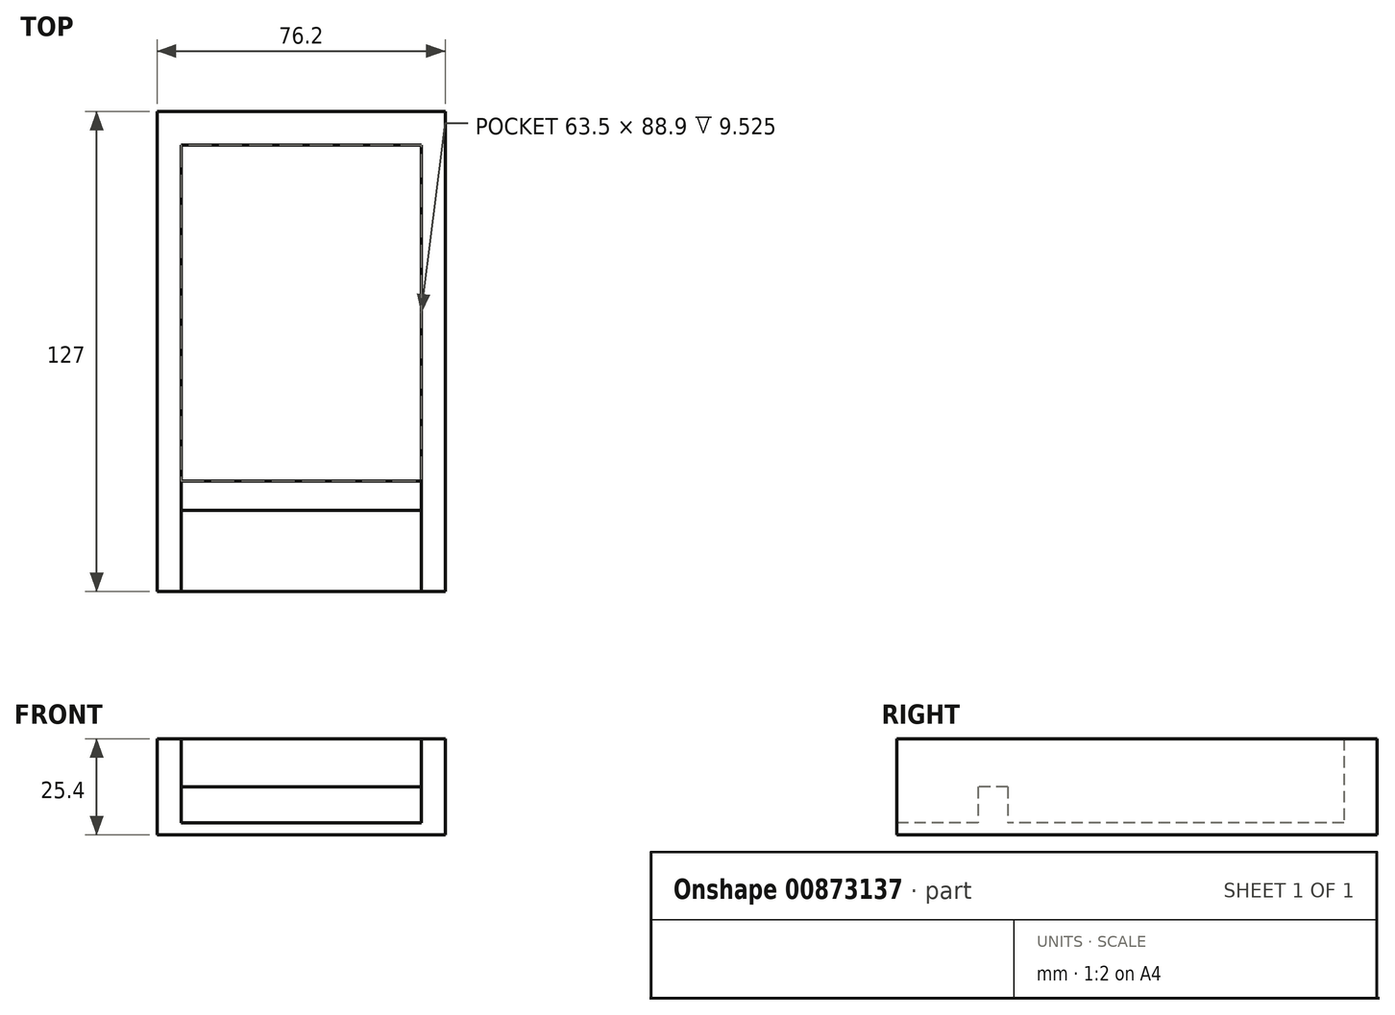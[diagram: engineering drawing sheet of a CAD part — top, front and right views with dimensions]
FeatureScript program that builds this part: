
annotation { "Feature Type Name" : "Feature", "Feature Type Description" : "" }
export const myFeature = defineFeature(function(context is Context, id is Id, definition is map)
    precondition{}
    {
        {
            var Q0;
            Q0=qCreatedBy(makeId("Top.planeOp"),FACE);
            var sketch = newSketch(context, id + "F0", { "sketchPlane" : qUnion([Q0])});
            skLineSegment(sketch, "E0.bottom", {"start": v(31.75, 44.45) * mm, "end": v(-31.75, 44.45) * mm});
            skLineSegment(sketch, "E0.top", {"start": v(31.75, -44.45) * mm, "end": v(-31.75, -44.45) * mm});
            skLineSegment(sketch, "E0.left", {"start": v(31.75, 44.45) * mm, "end": v(31.75, -44.45) * mm});
            skLineSegment(sketch, "E0.right", {"start": v(-31.75, 44.45) * mm, "end": v(-31.75, -44.45) * mm});
            skPoint(sketch, "E0.middle", {"position": v(0, 0) * mm});
            skLineSegment(sketch, "E1.bottom", {"start": v(38.1, 53.28) * mm, "end": v(-38.1, 53.28) * mm});
            skLineSegment(sketch, "E1.top", {"start": v(38.1, -73.72) * mm, "end": v(-38.1, -73.72) * mm});
            skLineSegment(sketch, "E1.left", {"start": v(38.1, 53.28) * mm, "end": v(38.1, -73.72) * mm});
            skLineSegment(sketch, "E1.right", {"start": v(-38.1, 53.28) * mm, "end": v(-38.1, -73.72) * mm});
            skPoint(sketch, "E1.middle", {"position": v(0, -10.22) * mm});
            skLineSegment(sketch, "E2.bottom", {"start": v(-31.75, -44.45) * mm, "end": v(31.75, -44.45) * mm});
            skLineSegment(sketch, "E2.top", {"start": v(-31.75, -52.29) * mm, "end": v(31.75, -52.29) * mm});
            skLineSegment(sketch, "E2.left", {"start": v(-31.75, -44.45) * mm, "end": v(-31.75, -52.29) * mm});
            skLineSegment(sketch, "E2.right", {"start": v(31.75, -44.45) * mm, "end": v(31.75, -52.29) * mm});
            skLineSegment(sketch, "E3.top", {"start": v(-31.75, -73.72) * mm, "end": v(31.75, -73.72) * mm});
            skLineSegment(sketch, "E3.left", {"start": v(-31.75, -52.29) * mm, "end": v(-31.75, -73.72) * mm});
            skLineSegment(sketch, "E3.right", {"start": v(31.75, -52.29) * mm, "end": v(31.75, -73.72) * mm});
            skSolve(sketch);
        }
        {
            var Q0;
            Q0=makeQuery(id+"F0.imprint","IMPRINT",FACE,{"disambiguationData":[TD([[makeQuery(id+"F0.imprint","IMPRINT",EDGE,{"derivedFrom":sQuery(id+"F0.wireOp",EDGE,"E2.top")}),-1.0]])]});
            extrude(context, id + "F1", {"entities" : qUnion([Q0]), "depth" : 3.17 * mm, "offsetDistance" : 25.4 * mm});
        }
        {
            var Q0;
            Q0=makeQuery(id+"F0.imprint","IMPRINT",FACE,{"disambiguationData":[TD([[makeQuery(id+"F0.imprint","IMPRINT",EDGE,{"derivedFrom":sQuery(id+"F0.wireOp",EDGE,"E0.bottom")}),-1.0]])]});
            extrude(context, id + "F2", {"entities" : qUnion([Q0]), "operationType" : NewBodyOperationType.ADD, "depth" : 25.4 * mm, "offsetDistance" : 25.4 * mm});
        }
        {
            var Q0;
            Q0=makeQuery(id+"F0.imprint","IMPRINT",FACE,{"disambiguationData":[TD([[makeQuery(id+"F0.imprint","IMPRINT",EDGE,{"derivedFrom":sQuery(id+"F0.wireOp",EDGE,"E0.top")}),1.0]])]});
            extrude(context, id + "F3", {"entities" : qUnion([Q0]), "operationType" : NewBodyOperationType.ADD, "depth" : 12.7 * mm, "offsetDistance" : 25.4 * mm});
        }
        {
            var Q0;
            Q0=makeQuery(id+"F0.imprint","IMPRINT",FACE,{"disambiguationData":[TD([[makeQuery(id+"F0.imprint","IMPRINT",EDGE,{"derivedFrom":sQuery(id+"F0.wireOp",EDGE,"E0.bottom")}),1.0]])]});
            extrude(context, id + "F4", {"entities" : qUnion([Q0]), "operationType" : NewBodyOperationType.ADD, "depth" : 3.17 * mm, "offsetDistance" : 25.4 * mm});
        }
    });
